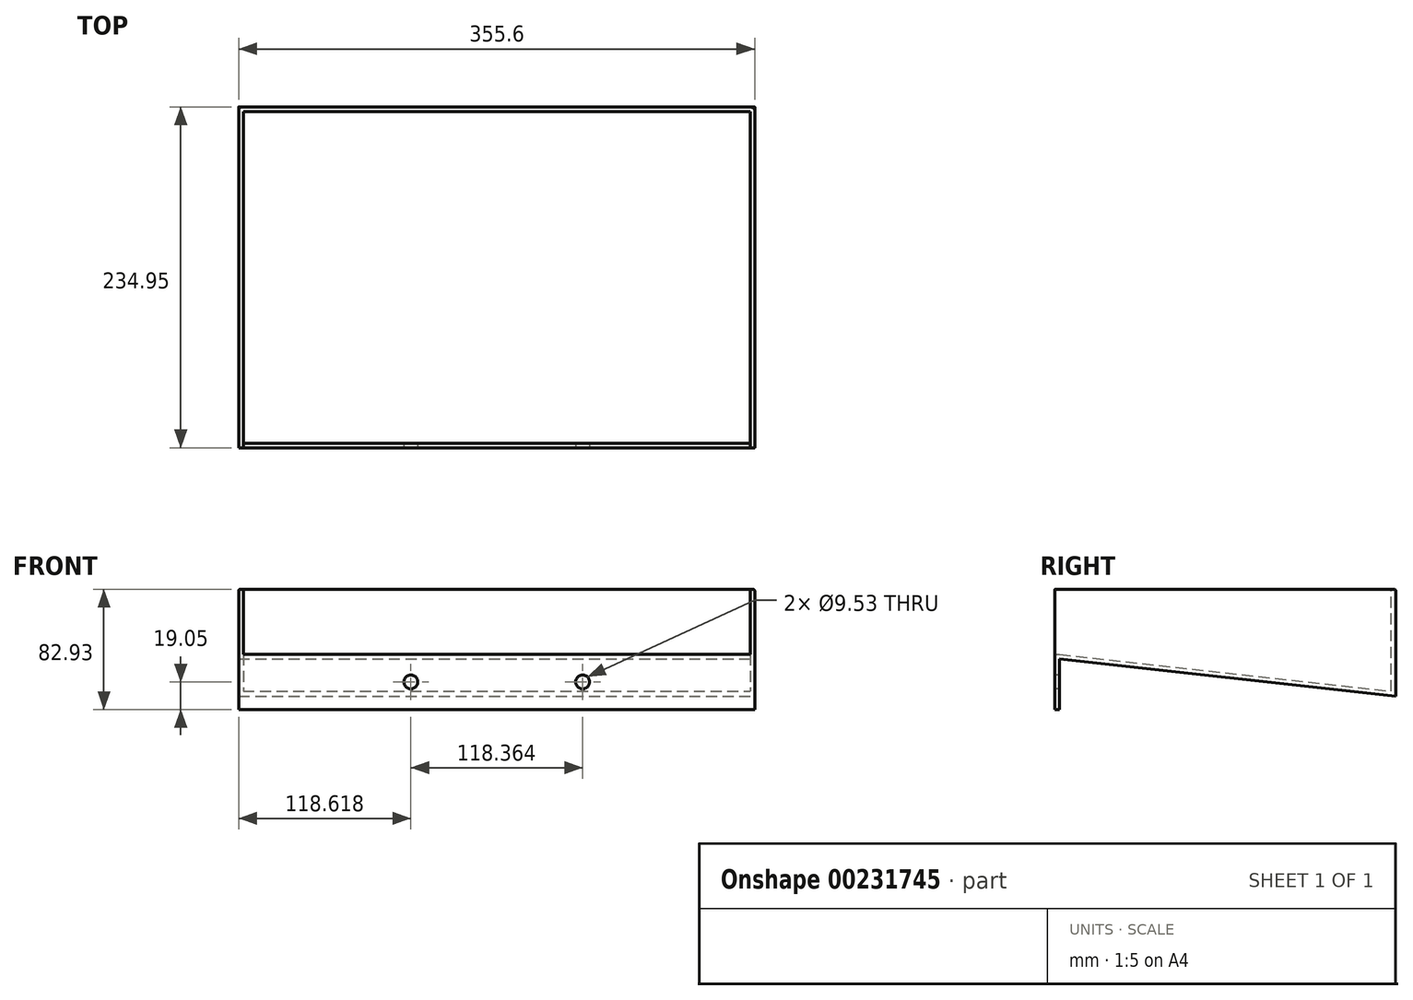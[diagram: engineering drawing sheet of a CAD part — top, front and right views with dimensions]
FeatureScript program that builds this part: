
annotation { "Feature Type Name" : "Feature", "Feature Type Description" : "" }
export const myFeature = defineFeature(function(context is Context, id is Id, definition is map)
    precondition{}
    {
        {
            var Q0;
            Q0=qCreatedBy(makeId("Right.planeOp"),FACE);
            var sketch = newSketch(context, id + "F0", { "sketchPlane" : qUnion([Q0])});
            skLineSegment(sketch, "E0", {"start": v(-110.08, 0) * mm, "end": v(118.52, 0) * mm, "construction": true});
            skLineSegment(sketch, "E1", {"start": v(-110.08, 0) * mm, "end": v(118.52, -25.4) * mm});
            skLineSegment(sketch, "E2", {"start": v(118.52, -25.4) * mm, "end": v(118.52, 44.83) * mm});
            skLineSegment(sketch, "E3", {"start": v(118.52, 44.83) * mm, "end": v(121.7, 44.83) * mm});
            skLineSegment(sketch, "E4", {"start": v(121.7, 44.83) * mm, "end": v(121.7, -28.93) * mm});
            skLineSegment(sketch, "E5", {"start": v(121.7, -28.93) * mm, "end": v(-110.08, -3.17) * mm});
            skLineSegment(sketch, "E6", {"start": v(-110.08, -3.18) * mm, "end": v(-110.08, 0) * mm});
            skLineSegment(sketch, "E7", {"start": v(-110.08, -3.18) * mm, "end": v(-110.08, -38.1) * mm});
            skLineSegment(sketch, "E8", {"start": v(-110.08, -38.1) * mm, "end": v(-113.26, -38.1) * mm});
            skLineSegment(sketch, "E9", {"start": v(-113.26, -38.1) * mm, "end": v(-113.26, 0) * mm});
            skLineSegment(sketch, "E10", {"start": v(-113.26, 0) * mm, "end": v(-110.08, 0) * mm});
            skSolve(sketch);
        }
        {
            var Q0;
            Q0=makeQuery(id+"F0.imprint","IMPRINT",FACE,{"disambiguationData":[TD([[makeQuery(id+"F0.imprint","IMPRINT",EDGE,{"derivedFrom":sQuery(id+"F0.wireOp",EDGE,"E1")}),-1.0]])]});
            var Q1;
            Q1=makeQuery(id+"F0.imprint","IMPRINT",FACE,{"disambiguationData":[TD([[makeQuery(id+"F0.imprint","IMPRINT",EDGE,{"derivedFrom":sQuery(id+"F0.wireOp",EDGE,"E6")}),1.0]])]});
            extrude(context, id + "F1", {"entities" : qUnion([Q0, Q1]), "oppositeDirection" : true, "depth" : 355.6 * mm});
        }
        {
            var Q0;
            Q0=qCreatedBy(makeId("Right.planeOp"),FACE);
            var sketch = newSketch(context, id + "F2", { "sketchPlane" : qUnion([Q0])});
            skLineSegment(sketch, "E11", {"start": v(-113.26, 0) * mm, "end": v(-113.26, 44.83) * mm});
            skLineSegment(sketch, "E12", {"start": v(-113.26, 44.83) * mm, "end": v(118.52, 44.83) * mm});
            skLineSegment(sketch, "E13", {"start": v(-113.26, 0) * mm, "end": v(-110.08, 0) * mm});
            skLineSegment(sketch, "E14", {"start": v(-110.08, 0) * mm, "end": v(118.52, -25.4) * mm});
            skLineSegment(sketch, "E15", {"start": v(118.52, -25.4) * mm, "end": v(118.52, 44.83) * mm});
            skSolve(sketch);
        }
        {
            var Q0;
            Q0=makeQuery(id+"F2.imprint","IMPRINT",FACE,{"disambiguationData":[TD([[makeQuery(id+"F2.imprint","IMPRINT",EDGE,{"derivedFrom":sQuery(id+"F2.wireOp",EDGE,"E11")}),-1.0]])]});
            extrude(context, id + "F3", {"entities" : qUnion([Q0]), "operationType" : NewBodyOperationType.ADD, "oppositeDirection" : true, "depth" : 3.17 * mm});
        }
        {
            var Q0;
            Q0=qCreatedBy(makeId("Right.planeOp"),FACE);
            cPlane(context, id + "F4", {"entities" : qUnion([Q0]), "cplaneType" : CPlaneType.OFFSET, "offset" : 355.6 * mm, "oppositeDirection" : true, "width" : 152.4 * mm, "height" : 152.4 * mm});
        }
        {
            var Q0;
            Q0=qCreatedBy(id+"F4.planeOp",FACE);
            var sketch = newSketch(context, id + "F5", { "sketchPlane" : qUnion([Q0])});
            skLineSegment(sketch, "E16", {"start": v(-113.26, 44.83) * mm, "end": v(118.52, 44.83) * mm});
            skLineSegment(sketch, "E17", {"start": v(-113.26, 44.83) * mm, "end": v(-113.26, 0) * mm});
            skLineSegment(sketch, "E18", {"start": v(-113.26, 0) * mm, "end": v(-110.08, 0) * mm});
            skLineSegment(sketch, "E19", {"start": v(-110.08, 0) * mm, "end": v(118.52, -25.4) * mm});
            skLineSegment(sketch, "E20", {"start": v(118.52, -25.4) * mm, "end": v(118.52, 44.83) * mm});
            skSolve(sketch);
        }
        {
            var Q0;
            Q0=makeQuery(id+"F5.imprint","IMPRINT",FACE,{"disambiguationData":[TD([[makeQuery(id+"F5.imprint","IMPRINT",EDGE,{"derivedFrom":sQuery(id+"F5.wireOp",EDGE,"E16")}),-1.0]])]});
            extrude(context, id + "F6", {"entities" : qUnion([Q0]), "operationType" : NewBodyOperationType.ADD, "depth" : 3.17 * mm});
        }
        {
            var Q0;
            Q0=makeQuery(id+"F6.boolean.opBoolean","MERGE",FACE,{"derivedFrom":[makeQuery(id+"F3.boolean.opBoolean","MERGE",FACE,{"derivedFrom":[makeQuery(id+"F1.opExtrude","SWEPT_FACE",FACE,{"disambiguationData":[OSD([sQuery(id+"F0.wireOp",EDGE,"E9")])]}),makeQuery(id+"F3.opExtrude","SWEPT_FACE",FACE,{"disambiguationData":[OSD([sQuery(id+"F2.wireOp",EDGE,"E11")])]})]}),makeQuery(id+"F6.opExtrude","SWEPT_FACE",FACE,{"disambiguationData":[OSD([sQuery(id+"F5.wireOp",EDGE,"E17")])]})]});
            var sketch = newSketch(context, id + "F7", { "sketchPlane" : qUnion([Q0])});
            skLineSegment(sketch, "E21", {"start": v(-355.6, -19.05) * mm, "end": v(0, -19.05) * mm, "construction": true});
            skCircle(sketch, "E22", {"center": v(-236.98, -19.05) * mm, "radius": 4.76 * mm});
            skCircle(sketch, "E23", {"center": v(-118.62, -19.05) * mm, "radius": 4.76 * mm});
            skSolve(sketch);
        }
        {
            var Q0;
            Q0=sQuery(id+"F7.wireOp",VERTEX,"E22.center");
            var Q1;
            Q1=sQuery(id+"F7.wireOp",VERTEX,"E23.center");
            var Q2;
            Q2=makeQuery(id+"F1.opExtrude","SWEPT_BODY",BODY,{"disambiguationData":[OSD([sQuery(id+"F0.wireOp",EDGE,"E1"),sQuery(id+"F0.wireOp",EDGE,"E2"),sQuery(id+"F0.wireOp",EDGE,"E3"),sQuery(id+"F0.wireOp",EDGE,"E4"),sQuery(id+"F0.wireOp",EDGE,"E5"),sQuery(id+"F0.wireOp",EDGE,"E7"),sQuery(id+"F0.wireOp",EDGE,"E8"),sQuery(id+"F0.wireOp",EDGE,"E9"),sQuery(id+"F0.wireOp",EDGE,"E10")])]});
            hole(context, id + "F8", {"style" : HoleStyle.SIMPLE, "endStyle" : HoleEndStyle.BLIND, "holeDiameter" : 9.52 * mm, "holeDepth" : 5.08 * mm, "locations" : qUnion([Q0, Q1]), "scope" : qUnion([Q2])});
        }
        {
            var Q0;
            Q0=makeQuery(id+"F6.opExtrude","CAP_EDGE",EDGE,{"disambiguationData":[OSD([sQuery(id+"F5.wireOp",EDGE,"E20")])],"isStart":false});
            var Q1;
            Q1=makeQuery(id+"F3.opExtrude","CAP_EDGE",EDGE,{"disambiguationData":[OSD([sQuery(id+"F2.wireOp",EDGE,"E15")])],"isStart":false});
            var Q2;
            Q2=makeQuery(id+"F6.opExtrude","CAP_EDGE",EDGE,{"disambiguationData":[OSD([sQuery(id+"F5.wireOp",EDGE,"E16")])],"isStart":true});
            var Q3;
            Q3=makeQuery(id+"F3.opExtrude","CAP_EDGE",EDGE,{"disambiguationData":[OSD([sQuery(id+"F2.wireOp",EDGE,"E12")])],"isStart":true});
            var Q4;
            Q4=makeQuery(id+"F1.opExtrude","SWEPT_EDGE",EDGE,{"disambiguationData":[OSD([sQuery(id+"F0.wireOp",EDGE,"E3"),sQuery(id+"F0.wireOp",EDGE,"E4")])]});
            fillet(context, id + "F9", {"entities" : qUnion([Q0, Q1, Q2, Q3, Q4]), "radius" : 1.27 * mm, "tangentPropagation" : true, "allowEdgeOverflow" : false});
        }
    });
